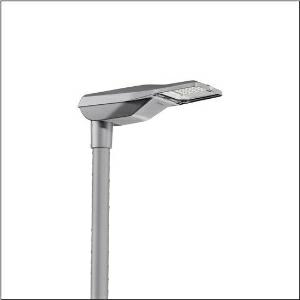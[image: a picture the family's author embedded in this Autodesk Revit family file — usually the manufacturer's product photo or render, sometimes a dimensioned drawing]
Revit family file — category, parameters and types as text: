
# Revit family: streetlight_sl_21_iq_micro___stw1_0a_5xe1e41d08cb_a1a9
name_source: partatom
category: Lighting Fixtures
units: mm (PartAtom-declared; Revit-internal decimal feet)

## family parameters
Cut with Voids When Loaded = No
Host = Face
Light Source = No
Part Type = Normal
Room Calculation Point = No
Round Connector Dimension = Use Diameter
Shared = No

## types (1)
- --- (1 x LED, 2980 lm, 19.4 W, 4000K)
    Apparent Load = 19 VA
    CIE Flux Codes = 38 75 98 100 100
    Color Rendering = 70
    Color Temperature = 4000K
    Default Elevation = 1800 mm
    Description = Streetlight SL 21 iQ micro, mast luminaire, primary light control with lens, of PMMA, primary optical cover: cover, of toughened safety glass, transparent, light distribution: STW1.0a, light emission: direct distribution, primary light characteristic: asymmetric, installation type: post-top, side-entry, LED, High Power LED, rated luminous flux: 2.980lm, luminous efficacy: 154lm/W, light colour: 740, colour temperature: 4000K, control gear: iQ-Comfort, control: Auto-Match, Temp-Guard, Lumen-Switch, Night-Set, Smart-Wire, Light-Fading, Desk-Remote (wireless, voltage-free reading and setting of iQ features in the workshop via application-optimized NFC function/RFID function), optimised constant luminous flux control (CLO 2.0), pre-setting: linear dimming characteristic, mains connection: 220..240V, AC, 50/60Hz, start of lifetime: 19W, end of service life: 20W, reduction: 10W, luminaire housing, of diecast aluminium, powder-coated, SITECO metallic grey (DB 702S), corrosivity category C5 high according to DIN EN ISO 12944, please order mast flange separately, inclination adjustable: 0°, 5°, 10°, 15°, sealing non-destructively replaceable, multi-level sealing system, length: 528mm, width: 235mm, height: 110mm, mast flange for spigot size: 42mm (side-entry): 5XC10008XM4, 60/48mm (side-entry/post-top): 5XC10108XM2, 76/60mm (side-entry/post-top): 5XC10108XM1, protection rating (complete): IP66, insulation class (complete): insulation class II (safety insulation), certification: CE, ENEC, ENEC+, VDE, impact resistance: IK10, permissible operating ambient temperature for outdoor applications: -40..+50°C, standard-compliant lighting for roads and squares, packaging unit: 1 piece

Light Distribution: STW1.0a
    Height = 110 mm
    Lamp = 1 x LED
    Lamp Light Flux = 2980 lm
    Lamp Power = 19.4 W
    Lamp count = 1
    Length = 528 mm
    Luminous efficacy = 154 lm/W
    Manufacturer = Siteco
    ModVariant = No
    Model = 5XE1E41D08CB
    Number of Poles = 1
    OnlyDefault = Yes
    Power Factor = 1
    Product Name = Streetlight SL 21 iQ micro | STW1.0a
    Product group = mast luminaire | pylon top
    ProductGroupID = 6100
    Protection Class = Protection class II
    Protection Degree = IP 66
    RLX_Detail_Level = 1
    RLX_Emergency_Light_Flux = 0 lm
    RLX_Emergency_Type = 0
    RLX_Emergency_Type_DB = No
    RlxData = <blob elided: 98609 chars, md5=1c3a1a8b>
    Socket = socket
    Standby Power = 0 W
    System Light Flux = 2980 lm
    System Power = 19 W
    Type Comments = factory setting: luminous flux: 100 % | dim-lin: 254 | 387 mA
    Type Image = l_1006881.jpg
    URL = http://relux.com
    VarID = @adj_138319
    Voltage = 0 V
    Weight = 0.00 kg
    Width = 235 mm

## geometry (parser evidence)
native form markers: Blend x4, Sweep x12
no freeform markers — native parametric forms only
